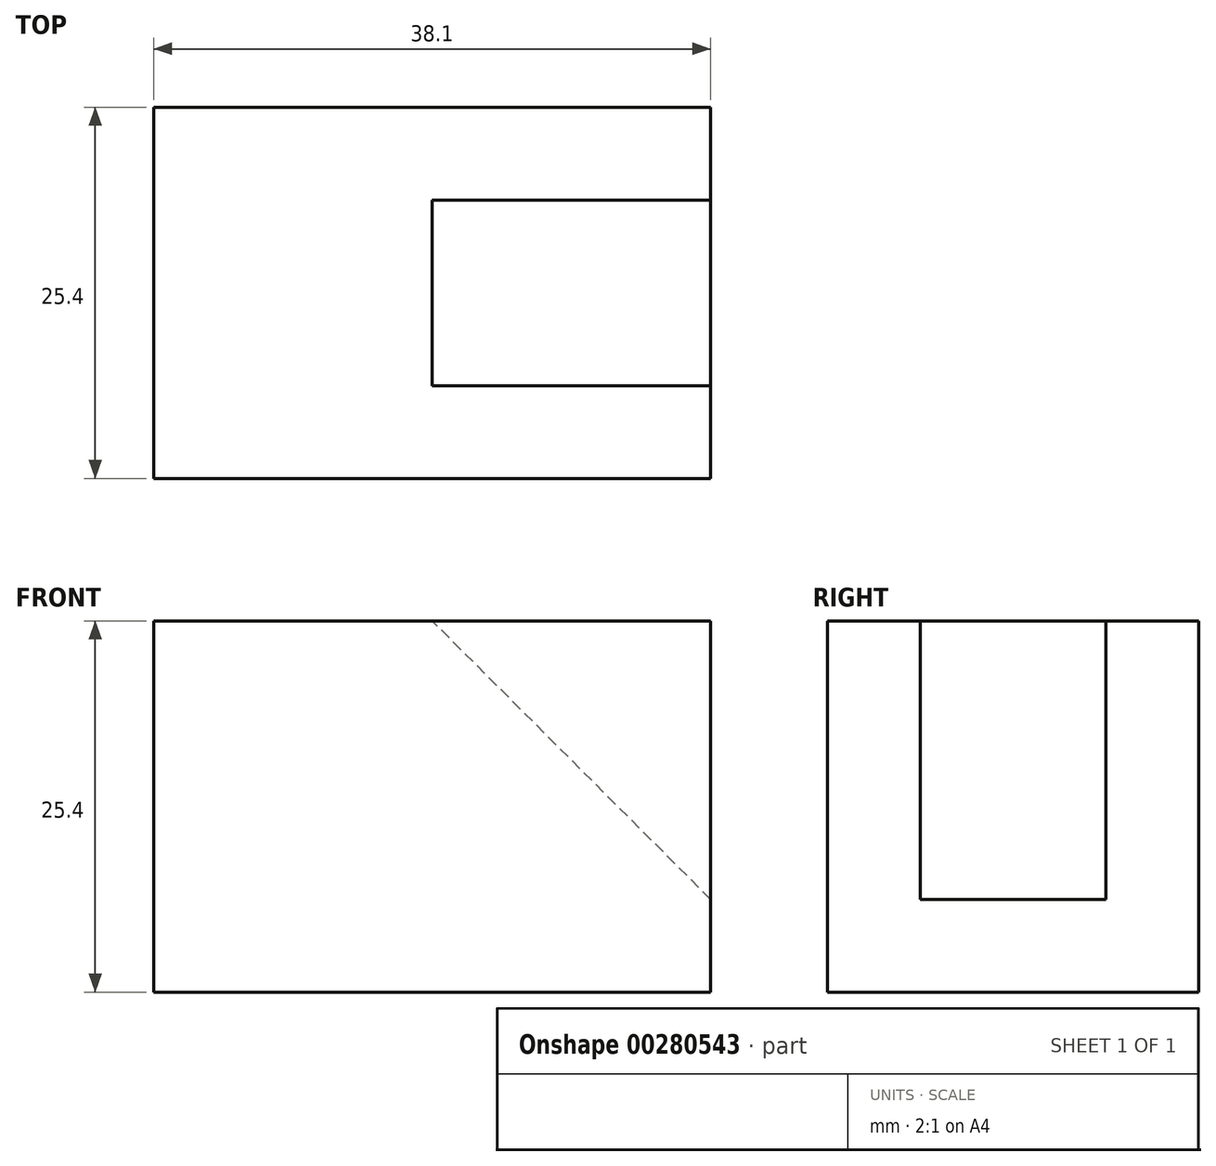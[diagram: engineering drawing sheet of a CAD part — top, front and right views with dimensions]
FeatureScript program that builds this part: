
annotation { "Feature Type Name" : "Feature", "Feature Type Description" : "" }
export const myFeature = defineFeature(function(context is Context, id is Id, definition is map)
    precondition{}
    {
        {
            var Q0;
            Q0=qCreatedBy(makeId("Top.planeOp"),FACE);
            var sketch = newSketch(context, id + "F0", { "sketchPlane" : qUnion([Q0])});
            skLineSegment(sketch, "E0", {"start": v(0, 0) * mm, "end": v(0, 25.4) * mm});
            skLineSegment(sketch, "E1", {"start": v(0, 25.4) * mm, "end": v(38.1, 25.4) * mm});
            skLineSegment(sketch, "E2", {"start": v(38.1, 25.4) * mm, "end": v(38.1, 19.05) * mm});
            skLineSegment(sketch, "E3", {"start": v(38.1, 19.05) * mm, "end": v(19.05, 19.05) * mm});
            skLineSegment(sketch, "E4", {"start": v(19.05, 19.05) * mm, "end": v(19.05, 6.35) * mm});
            skLineSegment(sketch, "E5", {"start": v(19.05, 6.35) * mm, "end": v(38.1, 6.35) * mm});
            skLineSegment(sketch, "E6", {"start": v(38.1, 6.35) * mm, "end": v(38.1, 0) * mm});
            skLineSegment(sketch, "E7", {"start": v(38.1, 0) * mm, "end": v(0, 0) * mm});
            skLineSegment(sketch, "E8", {"start": v(38.1, 19.05) * mm, "end": v(38.1, 6.35) * mm});
            skSolve(sketch);
        }
        {
            var Q0;
            Q0=makeQuery(id+"F0.imprint","IMPRINT",FACE,{"disambiguationData":[TD([[makeQuery(id+"F0.imprint","IMPRINT",EDGE,{"derivedFrom":sQuery(id+"F0.wireOp",EDGE,"E0")}),-1.0]])]});
            var Q1;
            Q1=makeQuery(id+"F0.imprint","IMPRINT",FACE,{"disambiguationData":[TD([[makeQuery(id+"F0.imprint","IMPRINT",EDGE,{"derivedFrom":sQuery(id+"F0.wireOp",EDGE,"E3")}),1.0]])]});
            extrude(context, id + "F1", {"entities" : qUnion([Q0, Q1]), "depth" : 25.4 * mm});
        }
        {
            var Q0;
            Q0=makeQuery(id+"F1.opExtrude","SWEPT_FACE",FACE,{"disambiguationData":[OSD([sQuery(id+"F0.wireOp",EDGE,"E7")])]});
            var sketch = newSketch(context, id + "F2", { "sketchPlane" : qUnion([Q0])});
            skLineSegment(sketch, "E9", {"start": v(19.05, 25.4) * mm, "end": v(38.1, 25.4) * mm});
            skLineSegment(sketch, "E10", {"start": v(38.1, 25.4) * mm, "end": v(38.1, 6.35) * mm});
            skLineSegment(sketch, "E11", {"start": v(38.1, 6.35) * mm, "end": v(19.05, 25.4) * mm});
            skSolve(sketch);
        }
        {
            var Q0;
            Q0=makeQuery(id+"F2.imprint","IMPRINT",FACE,{"disambiguationData":[TD([[makeQuery(id+"F2.imprint","IMPRINT",EDGE,{"derivedFrom":sQuery(id+"F2.wireOp",EDGE,"E9")}),1.0]])]});
            extrude(context, id + "F3", {"entities" : qUnion([Q0]), "operationType" : NewBodyOperationType.REMOVE, "oppositeDirection" : true, "depth" : 19.05 * mm, "hasSecondDirection" : true, "secondDirectionOppositeDirection" : true, "secondDirectionDepth" : 6.35 * mm});
        }
    });
